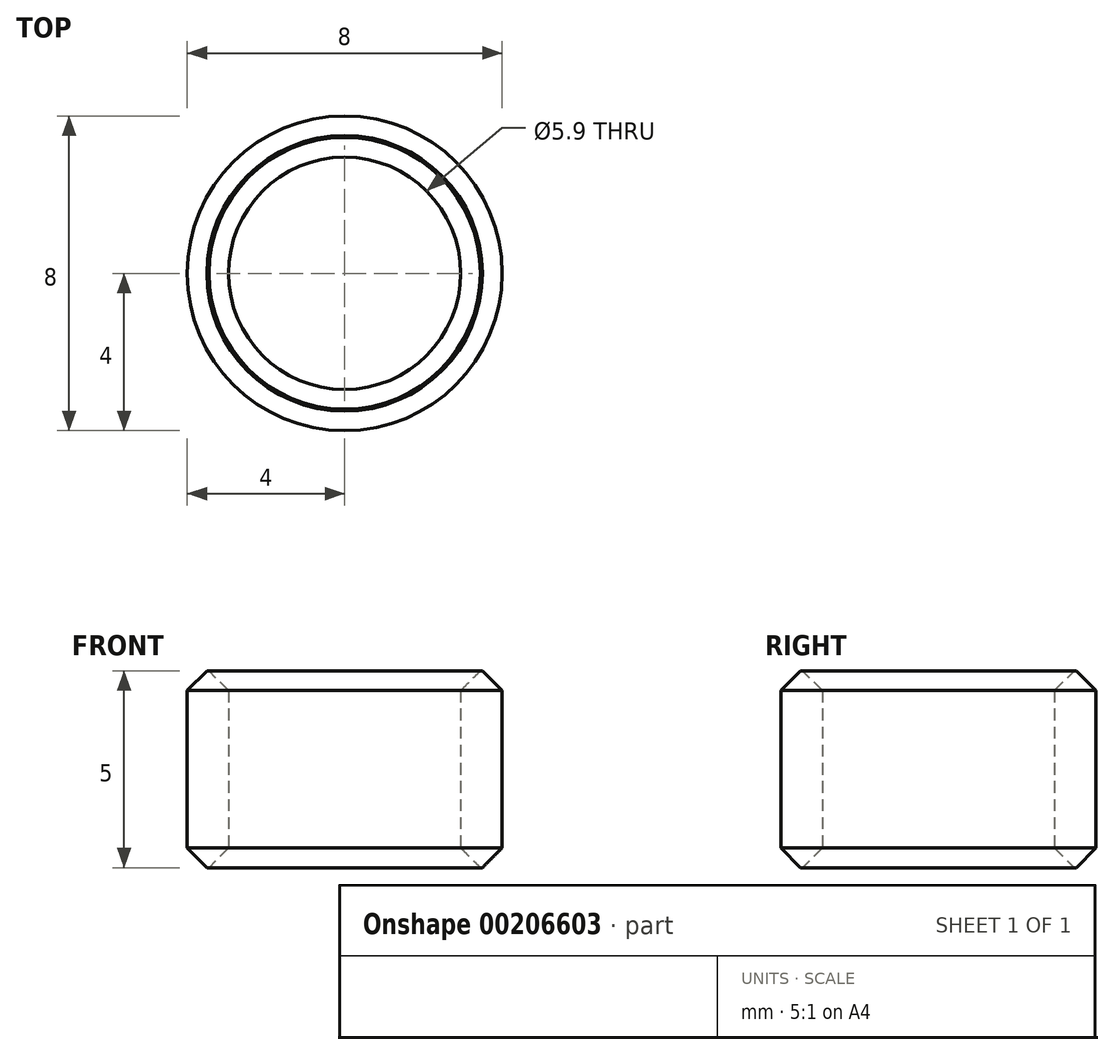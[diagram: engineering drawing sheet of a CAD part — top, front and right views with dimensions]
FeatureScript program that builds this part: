
annotation { "Feature Type Name" : "Feature", "Feature Type Description" : "" }
export const myFeature = defineFeature(function(context is Context, id is Id, definition is map)
    precondition{}
    {
        {
            var Q0;
            Q0=qCreatedBy(makeId("Top.planeOp"),FACE);
            var sketch = newSketch(context, id + "F0", { "sketchPlane" : qUnion([Q0])});
            skCircle(sketch, "E0", {"center": v(0, 0) * mm, "radius": 4 * mm});
            skCircle(sketch, "E1", {"center": v(0, 0) * mm, "radius": 2.95 * mm});
            skSolve(sketch);
        }
        {
            var Q0;
            Q0 = qSketchRegion(id + "F0", true);
            extrude(context, id + "F1", {"entities" : qUnion([Q0]), "depth" : 5 * mm});
        }
        {
            var Q0;
            Q0=makeQuery(id+"F1.opExtrude","CAP_EDGE",EDGE,{"disambiguationData":[OSD([sQuery(id+"F0.wireOp",EDGE,"E1")])],"isStart":false});
            var Q1;
            Q1=makeQuery(id+"F1.opExtrude","CAP_EDGE",EDGE,{"disambiguationData":[OSD([sQuery(id+"F0.wireOp",EDGE,"E0")])],"isStart":false});
            var Q2;
            Q2=makeQuery(id+"F1.opExtrude","CAP_EDGE",EDGE,{"disambiguationData":[OSD([sQuery(id+"F0.wireOp",EDGE,"E1")])],"isStart":true});
            var Q3;
            Q3=makeQuery(id+"F1.opExtrude","CAP_EDGE",EDGE,{"disambiguationData":[OSD([sQuery(id+"F0.wireOp",EDGE,"E0")])],"isStart":true});
            chamfer(context, id + "F2", {"entities" : qUnion([Q0, Q1, Q2, Q3]), "width" : .5 * mm, "tangentPropagation" : true});
        }
    });
